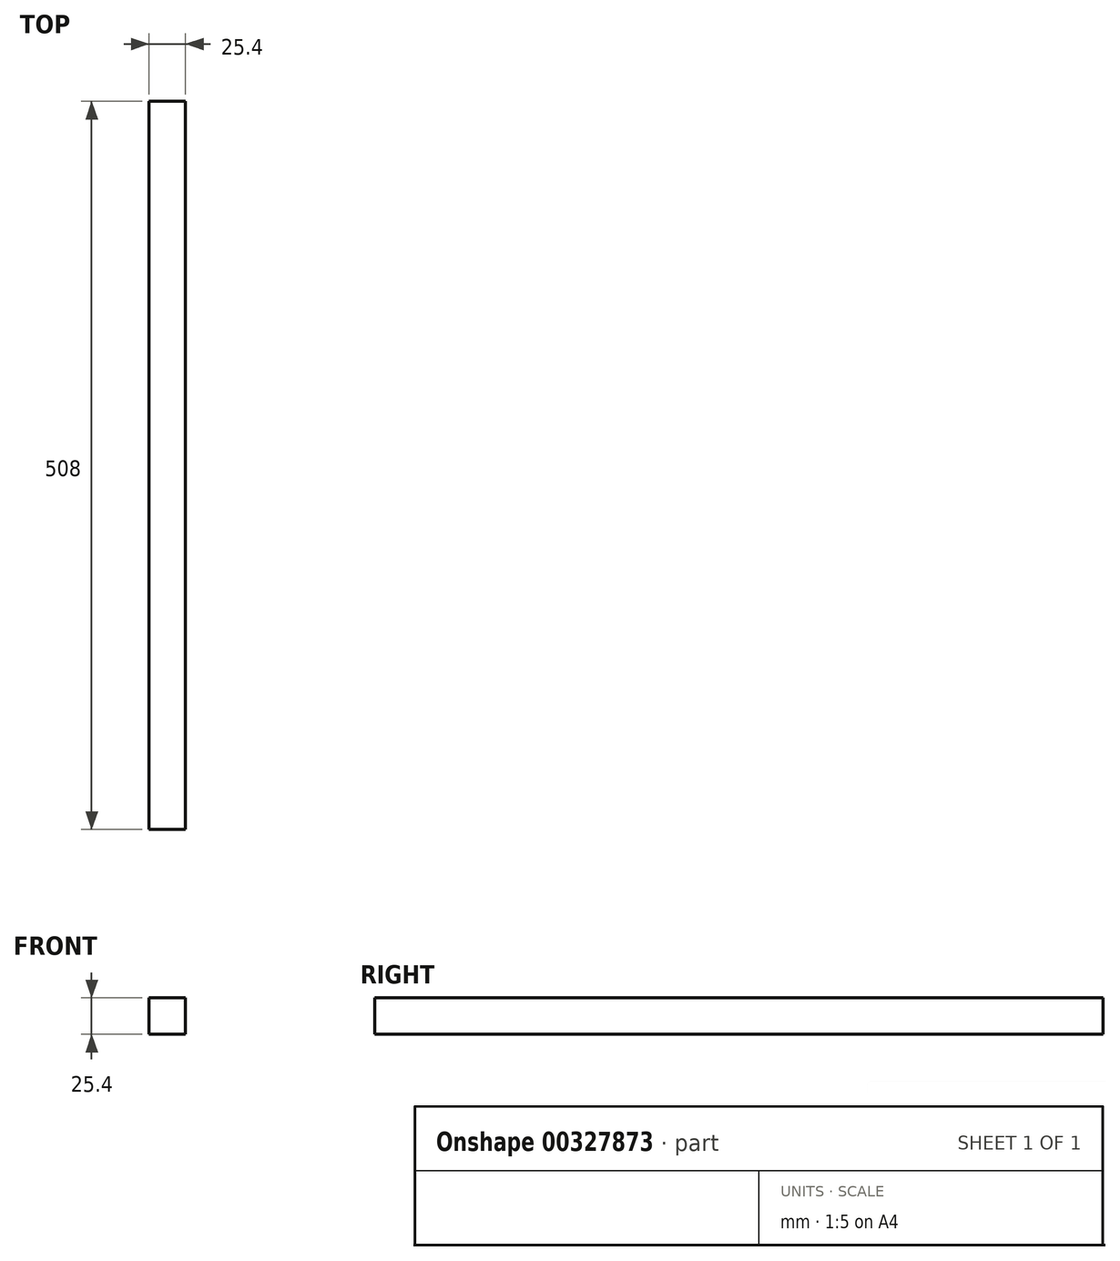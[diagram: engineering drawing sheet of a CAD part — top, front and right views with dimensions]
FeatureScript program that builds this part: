
annotation { "Feature Type Name" : "Feature", "Feature Type Description" : "" }
export const myFeature = defineFeature(function(context is Context, id is Id, definition is map)
    precondition{}
    {
        {
            var Q0;
            Q0=qCreatedBy(makeId("Front.planeOp"),FACE);
            var sketch = newSketch(context, id + "F0", { "sketchPlane" : qUnion([Q0])});
            skLineSegment(sketch, "E0.bottom", {"start": v(7.19, -9.09) * mm, "end": v(-18.21, -9.09) * mm});
            skLineSegment(sketch, "E0.top", {"start": v(7.19, 16.31) * mm, "end": v(-18.21, 16.31) * mm});
            skLineSegment(sketch, "E0.left", {"start": v(7.19, -9.09) * mm, "end": v(7.19, 16.31) * mm});
            skLineSegment(sketch, "E0.right", {"start": v(-18.21, -9.09) * mm, "end": v(-18.21, 16.31) * mm});
            skPoint(sketch, "E0.middle", {"position": v(-5.51, 3.61) * mm});
            skLineSegment(sketch, "E1.bottom", {"start": v(0, 0.87) * mm, "end": v(-11.03, 0.87) * mm});
            skLineSegment(sketch, "E1.top", {"start": v(0, 6.36) * mm, "end": v(-11.03, 6.36) * mm});
            skLineSegment(sketch, "E1.left", {"start": v(0, 0.87) * mm, "end": v(0, 6.36) * mm});
            skLineSegment(sketch, "E1.right", {"start": v(-11.03, 0.87) * mm, "end": v(-11.03, 6.36) * mm});
            skLineSegment(sketch, "E2", {"start": v(-11.03, 0.87) * mm, "end": v(-18.21, -9.09) * mm});
            skLineSegment(sketch, "E3", {"start": v(0, 0.87) * mm, "end": v(7.19, -9.09) * mm});
            skLineSegment(sketch, "E4", {"start": v(0, 6.36) * mm, "end": v(7.19, 16.31) * mm});
            skLineSegment(sketch, "E5", {"start": v(-11.03, 6.36) * mm, "end": v(-18.21, 16.31) * mm});
            skSolve(sketch);
        }
        {
            var Q0;
            Q0=makeQuery(id+"F0.imprint","IMPRINT",FACE,{"disambiguationData":[TD([[makeQuery(id+"F0.imprint","IMPRINT",EDGE,{"derivedFrom":sQuery(id+"F0.wireOp",EDGE,"E0.bottom")}),-1.0]])]});
            var Q1;
            Q1=makeQuery(id+"F0.imprint","IMPRINT",FACE,{"disambiguationData":[TD([[makeQuery(id+"F0.imprint","IMPRINT",EDGE,{"derivedFrom":sQuery(id+"F0.wireOp",EDGE,"E0.top")}),1.0]])]});
            var Q2;
            Q2=makeQuery(id+"F0.imprint","IMPRINT",FACE,{"disambiguationData":[TD([[makeQuery(id+"F0.imprint","IMPRINT",EDGE,{"derivedFrom":sQuery(id+"F0.wireOp",EDGE,"E0.left")}),1.0]])]});
            var Q3;
            Q3=makeQuery(id+"F0.imprint","IMPRINT",FACE,{"disambiguationData":[TD([[makeQuery(id+"F0.imprint","IMPRINT",EDGE,{"derivedFrom":sQuery(id+"F0.wireOp",EDGE,"E0.right")}),-1.0]])]});
            var Q4;
            Q4=makeQuery(id+"F0.imprint","IMPRINT",FACE,{"disambiguationData":[TD([[makeQuery(id+"F0.imprint","IMPRINT",EDGE,{"derivedFrom":sQuery(id+"F0.wireOp",EDGE,"E1.bottom")}),-1.0]])]});
            extrude(context, id + "F1", {"entities" : qUnion([Q0, Q1, Q2, Q3, Q4]), "depth" : 508 * mm});
        }
    });
